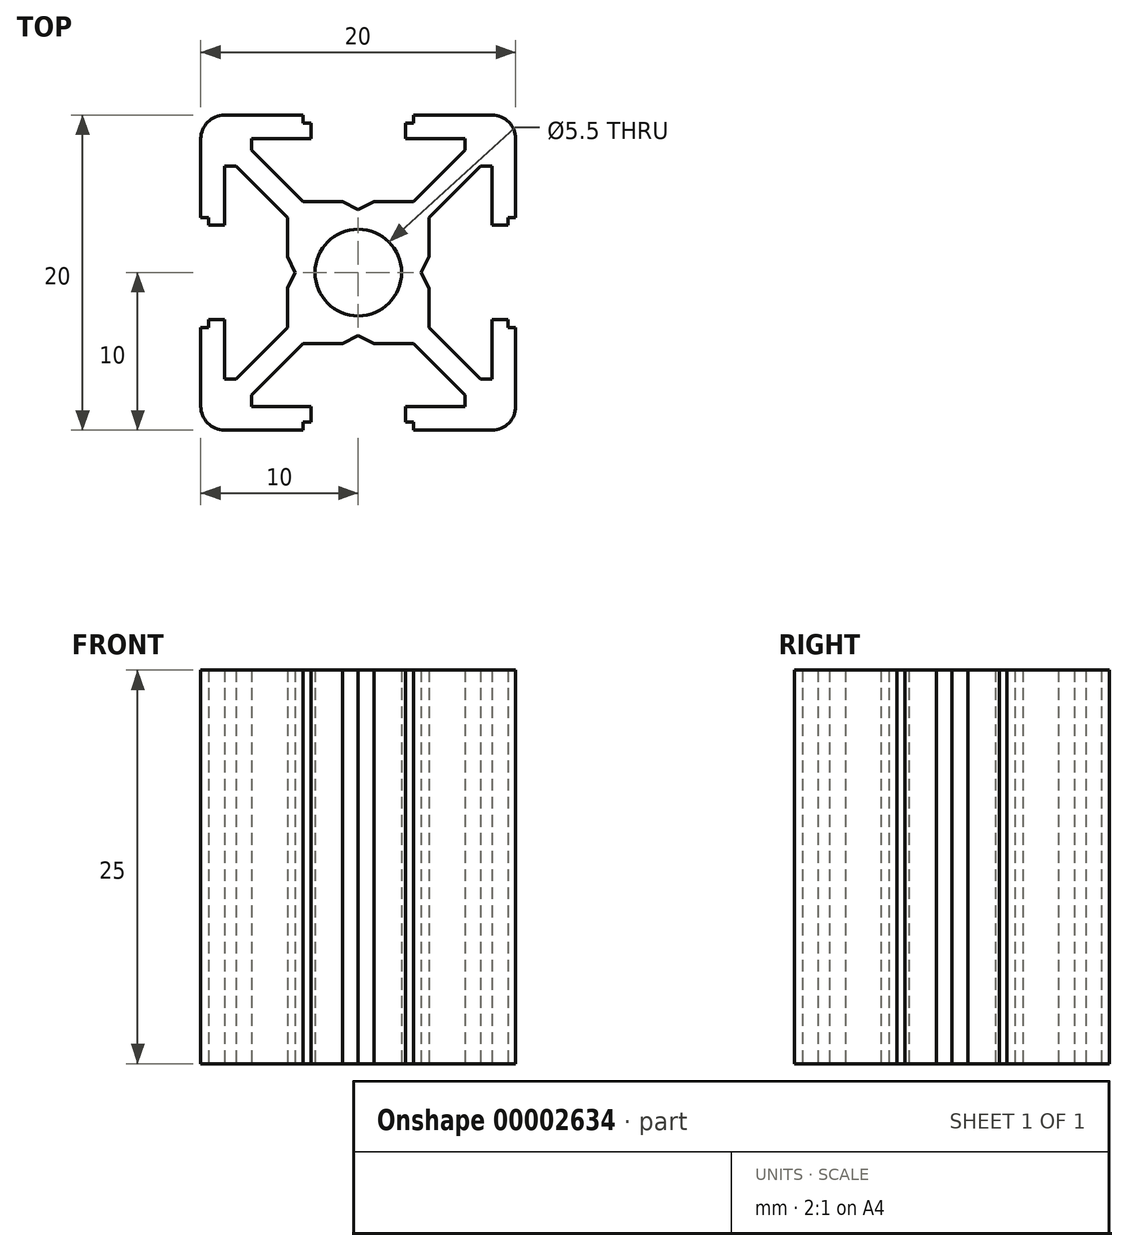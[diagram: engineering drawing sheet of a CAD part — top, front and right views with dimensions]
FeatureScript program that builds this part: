
annotation { "Feature Type Name" : "Feature", "Feature Type Description" : "" }
export const myFeature = defineFeature(function(context is Context, id is Id, definition is map)
    precondition{}
    {
        {
            var Q0;
            Q0=qCreatedBy(makeId("Top.planeOp"),FACE);
            var sketch = newSketch(context, id + "F0", { "sketchPlane" : qUnion([Q0])});
            skLineSegment(sketch, "E0", {"start": v(-1, -4.5) * mm, "end": v(-3.5, -4.5) * mm});
            skLineSegment(sketch, "E1", {"start": v(-6.77, -7.77) * mm, "end": v(-6.77, -8.5) * mm});
            skLineSegment(sketch, "E2", {"start": v(-6.77, -8.5) * mm, "end": v(-3, -8.5) * mm});
            skLineSegment(sketch, "E3", {"start": v(-3, -8.5) * mm, "end": v(-3, -9.5) * mm});
            skLineSegment(sketch, "E4", {"start": v(-5.56, -10) * mm, "end": v(-8.5, -10) * mm});
            skLineSegment(sketch, "E5", {"start": v(-1, -4.5) * mm, "end": v(0, -4) * mm});
            skLineSegment(sketch, "E6", {"start": v(-3, -9.5) * mm, "end": v(-3.5, -9.5) * mm});
            skLineSegment(sketch, "E7", {"start": v(-3.5, -9.5) * mm, "end": v(-3.5, -10) * mm, "construction": true});
            skArc(sketch, "E8.filletArc", {"start": v(-9.56, -9.56) * mm, "mid": v(-9.07, -9.89) * mm, "end": v(-8.5, -10) * mm});
            skLineSegment(sketch, "E9", {"start": v(-3.5, -10) * mm, "end": v(-5.56, -10) * mm});
            skPoint(sketch, "E10.orphan", {"position": v(0, -10) * mm});
            skLineSegment(sketch, "E11.trimOffspring", {"start": v(-8.5, -8.5) * mm, "end": v(-1.94, -1.94) * mm});
            skPoint(sketch, "E12", {"position": v(0, -4.5) * mm});
            skLineSegment(sketch, "E13", {"start": v(-3.5, -4.5) * mm, "end": v(-6.77, -7.77) * mm});
            skArc(sketch, "E14", {"start": v(-1.94, -1.94) * mm, "mid": v(-1.05, -2.54) * mm, "end": v(0, -2.75) * mm});
            skPoint(sketch, "E15", {"position": v(-1.94, -1.94) * mm});
            skLineSegment(sketch, "E16", {"start": v(0, -4) * mm, "end": v(0, -2.75) * mm});
            skLineSegment(sketch, "E17", {"start": v(-9.56, -9.56) * mm, "end": v(-8.5, -8.5) * mm});
            skPoint(sketch, "E18", {"position": v(-5.56, -10) * mm});
            skLineSegment(sketch, "E19", {"start": v(-3.5, -9.5) * mm, "end": v(-3.5, -10) * mm});
            skPoint(sketch, "E20.0.MirrorP", {"position": v(-10, -5.56) * mm});
            skPoint(sketch, "E20.1.MirrorP", {"position": v(-10, -5.56) * mm});
            skPoint(sketch, "E20.2.MirrorP", {"position": v(-10, -5.56) * mm});
            skPoint(sketch, "E20.3.MirrorP", {"position": v(-10, -5.56) * mm});
            skPoint(sketch, "E20.4.MirrorP", {"position": v(-10, -5.56) * mm});
            skPoint(sketch, "E20.5.MirrorP", {"position": v(-10, -5.56) * mm});
            skPoint(sketch, "E20.6.MirrorP", {"position": v(-10, -5.56) * mm});
            skPoint(sketch, "E20.7.MirrorP", {"position": v(-10, -5.56) * mm});
            skPoint(sketch, "E20.8.MirrorP", {"position": v(-10, -5.56) * mm});
            skPoint(sketch, "E20.9.MirrorP", {"position": v(-10, -5.56) * mm});
            skPoint(sketch, "E20.10.MirrorP", {"position": v(-10, -5.56) * mm});
            skLineSegment(sketch, "E20.11.MirrorCS", {"start": v(-9.5, -3.5) * mm, "end": v(-10, -3.5) * mm, "construction": true});
            skPoint(sketch, "E20.12.MirrorP", {"position": v(-10, -5.56) * mm});
            skLineSegment(sketch, "E20.13.MirrorCS", {"start": v(-9.5, -3.5) * mm, "end": v(-10, -3.5) * mm});
            skLineSegment(sketch, "E20.14.MirrorCS", {"start": v(-7.77, -6.77) * mm, "end": v(-8.5, -6.77) * mm});
            skPoint(sketch, "E20.15.MirrorP", {"position": v(-10, -5.56) * mm});
            skLineSegment(sketch, "E20.16.MirrorCS", {"start": v(-9.5, -3) * mm, "end": v(-9.5, -3.5) * mm});
            skPoint(sketch, "E20.17.MirrorP", {"position": v(-10, 0) * mm});
            skLineSegment(sketch, "E20.18.MirrorCS", {"start": v(-10, -5.56) * mm, "end": v(-10, -8.5) * mm});
            skArc(sketch, "E20.19.MirrorCS", {"start": v(-1.94, -1.94) * mm, "mid": v(-2.54, -1.05) * mm, "end": v(-2.75, 0) * mm});
            skPoint(sketch, "E20.20.MirrorP", {"position": v(-4.5, 0) * mm});
            skLineSegment(sketch, "E20.21.MirrorCS", {"start": v(-4.5, -3.5) * mm, "end": v(-7.77, -6.77) * mm});
            skLineSegment(sketch, "E20.23.MirrorCS", {"start": v(-4.5, -1) * mm, "end": v(-4.5, -3.5) * mm});
            skLineSegment(sketch, "E20.24.MirrorCS", {"start": v(-8.5, -6.77) * mm, "end": v(-8.5, -3) * mm});
            skLineSegment(sketch, "E20.25.MirrorCS", {"start": v(-10, -3.5) * mm, "end": v(-10, -5.56) * mm});
            skLineSegment(sketch, "E20.26.MirrorCS", {"start": v(-4, 0) * mm, "end": v(-2.75, 0) * mm});
            skArc(sketch, "E20.28.MirrorCS", {"start": v(-9.56, -9.56) * mm, "mid": v(-9.89, -9.07) * mm, "end": v(-10, -8.5) * mm});
            skLineSegment(sketch, "E20.29.MirrorCS", {"start": v(-4.5, -1) * mm, "end": v(-4, 0) * mm});
            skLineSegment(sketch, "E20.30.MirrorCS", {"start": v(-10, -5.56) * mm, "end": v(-10, -8.5) * mm});
            skPoint(sketch, "E20.31.MirrorP", {"position": v(-10, -5.56) * mm});
            skLineSegment(sketch, "E20.32.MirrorCS", {"start": v(-8.5, -3) * mm, "end": v(-9.5, -3) * mm});
            skPoint(sketch, "E21.0.MirrorP", {"position": v(-5.56, 10) * mm});
            skPoint(sketch, "E21.1.MirrorP", {"position": v(-10, 5.56) * mm});
            skPoint(sketch, "E21.2.MirrorP", {"position": v(-5.56, 10) * mm});
            skPoint(sketch, "E21.3.MirrorP", {"position": v(-10, 5.56) * mm});
            skPoint(sketch, "E21.4.MirrorP", {"position": v(-5.56, 10) * mm});
            skPoint(sketch, "E21.5.MirrorP", {"position": v(-10, 5.56) * mm});
            skPoint(sketch, "E21.6.MirrorP", {"position": v(-10, 5.56) * mm});
            skPoint(sketch, "E21.7.MirrorP", {"position": v(-5.56, 10) * mm});
            skPoint(sketch, "E21.8.MirrorP", {"position": v(-5.56, 10) * mm});
            skPoint(sketch, "E21.9.MirrorP", {"position": v(-10, 5.56) * mm});
            skPoint(sketch, "E21.10.MirrorP", {"position": v(-5.56, 10) * mm});
            skPoint(sketch, "E21.11.MirrorP", {"position": v(-10, 5.56) * mm});
            skPoint(sketch, "E21.12.MirrorP", {"position": v(-5.56, 10) * mm});
            skPoint(sketch, "E21.13.MirrorP", {"position": v(-10, 5.56) * mm});
            skPoint(sketch, "E21.14.MirrorP", {"position": v(-5.56, 10) * mm});
            skPoint(sketch, "E21.15.MirrorP", {"position": v(-10, 5.56) * mm});
            skPoint(sketch, "E21.16.MirrorP", {"position": v(-5.56, 10) * mm});
            skPoint(sketch, "E21.17.MirrorP", {"position": v(-10, 5.56) * mm});
            skLineSegment(sketch, "E21.18.MirrorCS", {"start": v(-9.5, 3.5) * mm, "end": v(-10, 3.5) * mm, "construction": true});
            skPoint(sketch, "E21.19.MirrorP", {"position": v(-5.56, 10) * mm});
            skPoint(sketch, "E21.20.MirrorP", {"position": v(-10, 5.56) * mm});
            skLineSegment(sketch, "E21.21.MirrorCS", {"start": v(-3.5, 9.5) * mm, "end": v(-3.5, 10) * mm, "construction": true});
            skLineSegment(sketch, "E21.22.MirrorCS", {"start": v(-3.5, 9.5) * mm, "end": v(-3.5, 10) * mm});
            skPoint(sketch, "E21.23.MirrorP", {"position": v(-5.56, 10) * mm});
            skLineSegment(sketch, "E21.24.MirrorCS", {"start": v(-9.5, 3.5) * mm, "end": v(-10, 3.5) * mm});
            skPoint(sketch, "E21.25.MirrorP", {"position": v(-10, 5.56) * mm});
            skPoint(sketch, "E21.26.MirrorP", {"position": v(-5.56, 10) * mm});
            skPoint(sketch, "E21.27.MirrorP", {"position": v(-10, 5.56) * mm});
            skLineSegment(sketch, "E21.28.MirrorCS", {"start": v(-3, 9.5) * mm, "end": v(-3.5, 9.5) * mm});
            skLineSegment(sketch, "E21.29.MirrorCS", {"start": v(-9.5, 3) * mm, "end": v(-9.5, 3.5) * mm});
            skLineSegment(sketch, "E21.30.MirrorCS", {"start": v(-8.5, 3) * mm, "end": v(-9.5, 3) * mm});
            skPoint(sketch, "E21.31.MirrorP", {"position": v(-5.56, 10) * mm});
            skPoint(sketch, "E21.32.MirrorP", {"position": v(-10, 5.56) * mm});
            skLineSegment(sketch, "E21.34.MirrorCS", {"start": v(-10, 3.5) * mm, "end": v(-10, 5.56) * mm});
            skArc(sketch, "E21.35.MirrorCS", {"start": v(-9.56, 9.56) * mm, "mid": v(-9.89, 9.07) * mm, "end": v(-10, 8.5) * mm});
            skLineSegment(sketch, "E21.36.MirrorCS", {"start": v(-8.5, 6.77) * mm, "end": v(-8.5, 3) * mm});
            skLineSegment(sketch, "E21.37.MirrorCS", {"start": v(-4.5, 1) * mm, "end": v(-4, 0) * mm});
            skLineSegment(sketch, "E21.38.MirrorCS", {"start": v(-10, 5.56) * mm, "end": v(-10, 8.5) * mm});
            skLineSegment(sketch, "E21.40.MirrorCS", {"start": v(-4.5, 3.5) * mm, "end": v(-7.77, 6.77) * mm});
            skLineSegment(sketch, "E21.41.MirrorCS", {"start": v(-4.5, 1) * mm, "end": v(-4.5, 3.5) * mm});
            skLineSegment(sketch, "E21.42.MirrorCS", {"start": v(-1, 4.5) * mm, "end": v(-3.5, 4.5) * mm});
            skLineSegment(sketch, "E21.43.MirrorCS", {"start": v(-6.77, 8.5) * mm, "end": v(-3, 8.5) * mm});
            skLineSegment(sketch, "E21.44.MirrorCS", {"start": v(-6.77, 7.77) * mm, "end": v(-6.77, 8.5) * mm});
            skLineSegment(sketch, "E21.45.MirrorCS", {"start": v(-5.56, 10) * mm, "end": v(-8.5, 10) * mm});
            skLineSegment(sketch, "E21.46.MirrorCS", {"start": v(-3, 8.5) * mm, "end": v(-3, 9.5) * mm});
            skLineSegment(sketch, "E21.47.MirrorCS", {"start": v(-1, 4.5) * mm, "end": v(0, 4) * mm});
            skLineSegment(sketch, "E21.48.MirrorCS", {"start": v(-5.56, 10) * mm, "end": v(-8.5, 10) * mm});
            skLineSegment(sketch, "E21.49.MirrorCS", {"start": v(-3.5, 10) * mm, "end": v(-5.56, 10) * mm});
            skArc(sketch, "E21.50.MirrorCS", {"start": v(-9.56, 9.56) * mm, "mid": v(-9.07, 9.89) * mm, "end": v(-8.5, 10) * mm});
            skLineSegment(sketch, "E21.51.MirrorCS", {"start": v(-3.5, 4.5) * mm, "end": v(-6.77, 7.77) * mm});
            skLineSegment(sketch, "E21.52.MirrorCS", {"start": v(-8.5, 8.5) * mm, "end": v(-1.94, 1.94) * mm});
            skLineSegment(sketch, "E21.53.MirrorCS", {"start": v(-9.56, 9.56) * mm, "end": v(-8.5, 8.5) * mm});
            skLineSegment(sketch, "E21.54.MirrorCS", {"start": v(-9.56, 9.56) * mm, "end": v(-8.5, 8.5) * mm});
            skLineSegment(sketch, "E21.55.MirrorCS", {"start": v(0, 4) * mm, "end": v(0, 2.75) * mm});
            skArc(sketch, "E21.56.MirrorCS", {"start": v(-1.94, 1.94) * mm, "mid": v(-1.05, 2.54) * mm, "end": v(0, 2.75) * mm});
            skPoint(sketch, "E21.58.MirrorP", {"position": v(0, 4.5) * mm});
            skLineSegment(sketch, "E21.59.MirrorCS", {"start": v(-7.77, 6.77) * mm, "end": v(-8.5, 6.77) * mm});
            skPoint(sketch, "E21.60.MirrorP", {"position": v(-5.56, 10) * mm});
            skArc(sketch, "E21.61.MirrorCS", {"start": v(-1.94, 1.94) * mm, "mid": v(-2.54, 1.05) * mm, "end": v(-2.75, 0) * mm});
            skPoint(sketch, "E21.62.MirrorP", {"position": v(0, 10) * mm});
            skPoint(sketch, "E21.63.MirrorP", {"position": v(-1.94, 1.94) * mm});
            skPoint(sketch, "E21.64.MirrorP", {"position": v(-1.94, 1.94) * mm});
            skLineSegment(sketch, "E21.65.MirrorCS", {"start": v(-10, 5.56) * mm, "end": v(-10, 8.5) * mm});
            skPoint(sketch, "E21.66.MirrorP", {"position": v(-10, 5.56) * mm});
            skPoint(sketch, "E22.0.MirrorP", {"position": v(10, 5.56) * mm});
            skPoint(sketch, "E22.1.MirrorP", {"position": v(5.56, -10) * mm});
            skPoint(sketch, "E22.2.MirrorP", {"position": v(5.56, 10) * mm});
            skPoint(sketch, "E22.3.MirrorP", {"position": v(10, 5.56) * mm});
            skPoint(sketch, "E22.4.MirrorP", {"position": v(10, -5.56) * mm});
            skPoint(sketch, "E22.5.MirrorP", {"position": v(5.56, -10) * mm});
            skPoint(sketch, "E22.6.MirrorP", {"position": v(5.56, -10) * mm});
            skPoint(sketch, "E22.7.MirrorP", {"position": v(10, 5.56) * mm});
            skPoint(sketch, "E22.8.MirrorP", {"position": v(5.56, 10) * mm});
            skPoint(sketch, "E22.9.MirrorP", {"position": v(10, -5.56) * mm});
            skPoint(sketch, "E22.10.MirrorP", {"position": v(10, 5.56) * mm});
            skPoint(sketch, "E22.11.MirrorP", {"position": v(5.56, -10) * mm});
            skPoint(sketch, "E22.12.MirrorP", {"position": v(5.56, 10) * mm});
            skPoint(sketch, "E22.13.MirrorP", {"position": v(10, -5.56) * mm});
            skPoint(sketch, "E22.14.MirrorP", {"position": v(10, 5.56) * mm});
            skPoint(sketch, "E22.15.MirrorP", {"position": v(5.56, -10) * mm});
            skPoint(sketch, "E22.16.MirrorP", {"position": v(10, -5.56) * mm});
            skPoint(sketch, "E22.17.MirrorP", {"position": v(5.56, 10) * mm});
            skPoint(sketch, "E22.18.MirrorP", {"position": v(5.56, -10) * mm});
            skPoint(sketch, "E22.19.MirrorP", {"position": v(5.56, 10) * mm});
            skPoint(sketch, "E22.20.MirrorP", {"position": v(10, 5.56) * mm});
            skPoint(sketch, "E22.21.MirrorP", {"position": v(10, -5.56) * mm});
            skPoint(sketch, "E22.22.MirrorP", {"position": v(10, -5.56) * mm});
            skPoint(sketch, "E22.23.MirrorP", {"position": v(5.56, -10) * mm});
            skPoint(sketch, "E22.24.MirrorP", {"position": v(10, 5.56) * mm});
            skPoint(sketch, "E22.25.MirrorP", {"position": v(5.56, 10) * mm});
            skPoint(sketch, "E22.26.MirrorP", {"position": v(10, -5.56) * mm});
            skPoint(sketch, "E22.27.MirrorP", {"position": v(10, 5.56) * mm});
            skPoint(sketch, "E22.28.MirrorP", {"position": v(5.56, -10) * mm});
            skPoint(sketch, "E22.29.MirrorP", {"position": v(5.56, 10) * mm});
            skPoint(sketch, "E22.30.MirrorP", {"position": v(10, -5.56) * mm});
            skPoint(sketch, "E22.31.MirrorP", {"position": v(5.56, 10) * mm});
            skPoint(sketch, "E22.32.MirrorP", {"position": v(5.56, -10) * mm});
            skPoint(sketch, "E22.33.MirrorP", {"position": v(10, 5.56) * mm});
            skPoint(sketch, "E22.34.MirrorP", {"position": v(10, 5.56) * mm});
            skPoint(sketch, "E22.35.MirrorP", {"position": v(5.56, 10) * mm});
            skPoint(sketch, "E22.36.MirrorP", {"position": v(10, -5.56) * mm});
            skPoint(sketch, "E22.37.MirrorP", {"position": v(5.56, -10) * mm});
            skLineSegment(sketch, "E22.38.MirrorCS", {"start": v(3.5, 9.5) * mm, "end": v(3.5, 10) * mm, "construction": true});
            skLineSegment(sketch, "E22.39.MirrorCS", {"start": v(9.5, 3.5) * mm, "end": v(10, 3.5) * mm, "construction": true});
            skLineSegment(sketch, "E22.40.MirrorCS", {"start": v(9.5, -3.5) * mm, "end": v(10, -3.5) * mm, "construction": true});
            skLineSegment(sketch, "E22.41.MirrorCS", {"start": v(3.5, -9.5) * mm, "end": v(3.5, -10) * mm, "construction": true});
            skPoint(sketch, "E22.42.MirrorP", {"position": v(10, 5.56) * mm});
            skPoint(sketch, "E22.43.MirrorP", {"position": v(10, -5.56) * mm});
            skPoint(sketch, "E22.44.MirrorP", {"position": v(5.56, -10) * mm});
            skPoint(sketch, "E22.45.MirrorP", {"position": v(5.56, 10) * mm});
            skLineSegment(sketch, "E22.46.MirrorCS", {"start": v(9.5, 3.5) * mm, "end": v(10, 3.5) * mm});
            skLineSegment(sketch, "E22.47.MirrorCS", {"start": v(9.5, -3) * mm, "end": v(9.5, -3.5) * mm});
            skLineSegment(sketch, "E22.48.MirrorCS", {"start": v(9.5, -3.5) * mm, "end": v(10, -3.5) * mm});
            skLineSegment(sketch, "E22.49.MirrorCS", {"start": v(9.56, -9.56) * mm, "end": v(8.5, -8.5) * mm});
            skLineSegment(sketch, "E22.50.MirrorCS", {"start": v(3, -9.5) * mm, "end": v(3.5, -9.5) * mm});
            skPoint(sketch, "E22.51.MirrorP", {"position": v(10, -5.56) * mm});
            skPoint(sketch, "E22.52.MirrorP", {"position": v(10, 5.56) * mm});
            skPoint(sketch, "E22.53.MirrorP", {"position": v(5.56, 10) * mm});
            skPoint(sketch, "E22.54.MirrorP", {"position": v(5.56, -10) * mm});
            skLineSegment(sketch, "E22.55.MirrorCS", {"start": v(3, 9.5) * mm, "end": v(3.5, 9.5) * mm});
            skLineSegment(sketch, "E22.56.MirrorCS", {"start": v(9.5, 3) * mm, "end": v(9.5, 3.5) * mm});
            skLineSegment(sketch, "E22.57.MirrorCS", {"start": v(3.5, -9.5) * mm, "end": v(3.5, -10) * mm});
            skLineSegment(sketch, "E22.58.MirrorCS", {"start": v(3.5, 9.5) * mm, "end": v(3.5, 10) * mm});
            skLineSegment(sketch, "E22.59.MirrorCS", {"start": v(3, 8.5) * mm, "end": v(3, 9.5) * mm});
            skLineSegment(sketch, "E22.60.MirrorCS", {"start": v(6.77, 7.77) * mm, "end": v(6.77, 8.5) * mm});
            skPoint(sketch, "E22.61.MirrorP", {"position": v(5.56, 10) * mm});
            skLineSegment(sketch, "E22.62.MirrorCS", {"start": v(6.77, -7.77) * mm, "end": v(6.77, -8.5) * mm});
            skPoint(sketch, "E22.63.MirrorP", {"position": v(5.56, -10) * mm});
            skPoint(sketch, "E22.64.MirrorP", {"position": v(10, -5.56) * mm});
            skLineSegment(sketch, "E22.65.MirrorCS", {"start": v(9.56, -9.56) * mm, "end": v(8.5, -8.5) * mm});
            skLineSegment(sketch, "E22.66.MirrorCS", {"start": v(7.77, 6.77) * mm, "end": v(8.5, 6.77) * mm});
            skLineSegment(sketch, "E22.67.MirrorCS", {"start": v(1, 4.5) * mm, "end": v(0, 4) * mm});
            skLineSegment(sketch, "E22.68.MirrorCS", {"start": v(4.5, -1) * mm, "end": v(4, 0) * mm});
            skLineSegment(sketch, "E22.69.MirrorCS", {"start": v(4, 0) * mm, "end": v(2.75, 0) * mm});
            skLineSegment(sketch, "E22.70.MirrorCS", {"start": v(1, -4.5) * mm, "end": v(0, -4) * mm});
            skLineSegment(sketch, "E22.71.MirrorCS", {"start": v(10, 5.56) * mm, "end": v(10, 8.5) * mm});
            skPoint(sketch, "E22.72.MirrorP", {"position": v(10, 5.56) * mm});
            skPoint(sketch, "E22.73.MirrorP", {"position": v(10, 0) * mm});
            skLineSegment(sketch, "E22.74.MirrorCS", {"start": v(9.56, 9.56) * mm, "end": v(8.5, 8.5) * mm});
            skLineSegment(sketch, "E22.75.MirrorCS", {"start": v(4.5, 1) * mm, "end": v(4, 0) * mm});
            skLineSegment(sketch, "E22.76.MirrorCS", {"start": v(7.77, -6.77) * mm, "end": v(8.5, -6.77) * mm});
            skLineSegment(sketch, "E22.78.MirrorCS", {"start": v(10, 5.56) * mm, "end": v(10, 8.5) * mm});
            skLineSegment(sketch, "E22.79.MirrorCS", {"start": v(3.5, -10) * mm, "end": v(5.56, -10) * mm});
            skLineSegment(sketch, "E22.80.MirrorCS", {"start": v(3, -8.5) * mm, "end": v(3, -9.5) * mm});
            skLineSegment(sketch, "E22.81.MirrorCS", {"start": v(5.56, -10) * mm, "end": v(8.5, -10) * mm});
            skPoint(sketch, "E22.83.MirrorP", {"position": v(5.56, -10) * mm});
            skLineSegment(sketch, "E22.84.MirrorCS", {"start": v(8.5, 3) * mm, "end": v(9.5, 3) * mm});
            skLineSegment(sketch, "E22.85.MirrorCS", {"start": v(3.5, 10) * mm, "end": v(5.56, 10) * mm});
            skArc(sketch, "E22.86.MirrorCS", {"start": v(1.94, -1.94) * mm, "mid": v(1.05, -2.54) * mm, "end": v(0, -2.75) * mm});
            skPoint(sketch, "E22.87.MirrorP", {"position": v(1.94, -1.94) * mm});
            skPoint(sketch, "E22.88.MirrorP", {"position": v(4.5, 0) * mm});
            skArc(sketch, "E22.89.MirrorCS", {"start": v(9.56, 9.56) * mm, "mid": v(9.07, 9.89) * mm, "end": v(8.5, 10) * mm});
            skLineSegment(sketch, "E22.90.MirrorCS", {"start": v(10, 3.5) * mm, "end": v(10, 5.56) * mm});
            skLineSegment(sketch, "E22.91.MirrorCS", {"start": v(8.5, -8.5) * mm, "end": v(1.94, -1.94) * mm});
            skLineSegment(sketch, "E22.92.MirrorCS", {"start": v(3.5, -4.5) * mm, "end": v(6.77, -7.77) * mm});
            skArc(sketch, "E22.93.MirrorCS", {"start": v(9.56, -9.56) * mm, "mid": v(9.07, -9.89) * mm, "end": v(8.5, -10) * mm});
            skLineSegment(sketch, "E22.94.MirrorCS", {"start": v(6.77, 8.5) * mm, "end": v(3, 8.5) * mm});
            skLineSegment(sketch, "E22.95.MirrorCS", {"start": v(4.5, 1) * mm, "end": v(4.5, 3.5) * mm});
            skLineSegment(sketch, "E22.96.MirrorCS", {"start": v(10, -5.56) * mm, "end": v(10, -8.5) * mm});
            skLineSegment(sketch, "E22.97.MirrorCS", {"start": v(5.56, -10) * mm, "end": v(8.5, -10) * mm});
            skPoint(sketch, "E22.99.MirrorP", {"position": v(5.56, 10) * mm});
            skLineSegment(sketch, "E22.101.MirrorCS", {"start": v(10, -5.56) * mm, "end": v(10, -8.5) * mm});
            skPoint(sketch, "E22.103.MirrorP", {"position": v(4.5, 0) * mm});
            skArc(sketch, "E22.104.MirrorCS", {"start": v(1.94, 1.94) * mm, "mid": v(1.05, 2.54) * mm, "end": v(0, 2.75) * mm});
            skArc(sketch, "E22.105.MirrorCS", {"start": v(1.94, -1.94) * mm, "mid": v(2.54, -1.05) * mm, "end": v(2.75, 0) * mm});
            skLineSegment(sketch, "E22.106.MirrorCS", {"start": v(4.5, 3.5) * mm, "end": v(7.77, 6.77) * mm});
            skLineSegment(sketch, "E22.107.MirrorCS", {"start": v(8.5, 8.5) * mm, "end": v(1.94, 1.94) * mm});
            skLineSegment(sketch, "E22.108.MirrorCS", {"start": v(8.5, -6.77) * mm, "end": v(8.5, -3) * mm});
            skArc(sketch, "E22.109.MirrorCS", {"start": v(9.56, -9.56) * mm, "mid": v(9.89, -9.07) * mm, "end": v(10, -8.5) * mm});
            skPoint(sketch, "E22.110.MirrorP", {"position": v(1.94, 1.94) * mm});
            skLineSegment(sketch, "E22.111.MirrorCS", {"start": v(6.77, -8.5) * mm, "end": v(3, -8.5) * mm});
            skLineSegment(sketch, "E22.112.MirrorCS", {"start": v(1, -4.5) * mm, "end": v(3.5, -4.5) * mm});
            skLineSegment(sketch, "E22.113.MirrorCS", {"start": v(4.5, -1) * mm, "end": v(4.5, -3.5) * mm});
            skLineSegment(sketch, "E22.114.MirrorCS", {"start": v(3.5, 4.5) * mm, "end": v(6.77, 7.77) * mm});
            skPoint(sketch, "E22.115.MirrorP", {"position": v(10, -5.56) * mm});
            skLineSegment(sketch, "E22.116.MirrorCS", {"start": v(9.56, 9.56) * mm, "end": v(8.5, 8.5) * mm});
            skLineSegment(sketch, "E22.117.MirrorCS", {"start": v(4, 0) * mm, "end": v(2.75, 0) * mm});
            skArc(sketch, "E22.118.MirrorCS", {"start": v(9.56, 9.56) * mm, "mid": v(9.89, 9.07) * mm, "end": v(10, 8.5) * mm});
            skPoint(sketch, "E22.119.MirrorP", {"position": v(5.56, 10) * mm});
            skLineSegment(sketch, "E22.120.MirrorCS", {"start": v(8.5, -3) * mm, "end": v(9.5, -3) * mm});
            skLineSegment(sketch, "E22.121.MirrorCS", {"start": v(1, 4.5) * mm, "end": v(3.5, 4.5) * mm});
            skArc(sketch, "E22.122.MirrorCS", {"start": v(1.94, 1.94) * mm, "mid": v(2.54, 1.05) * mm, "end": v(2.75, 0) * mm});
            skLineSegment(sketch, "E22.123.MirrorCS", {"start": v(5.56, 10) * mm, "end": v(8.5, 10) * mm});
            skPoint(sketch, "E22.124.MirrorP", {"position": v(10, 0) * mm});
            skLineSegment(sketch, "E22.125.MirrorCS", {"start": v(10, -3.5) * mm, "end": v(10, -5.56) * mm});
            skLineSegment(sketch, "E22.126.MirrorCS", {"start": v(5.56, 10) * mm, "end": v(8.5, 10) * mm});
            skLineSegment(sketch, "E22.127.MirrorCS", {"start": v(4.5, -3.5) * mm, "end": v(7.77, -6.77) * mm});
            skPoint(sketch, "E22.128.MirrorP", {"position": v(10, -5.56) * mm});
            skPoint(sketch, "E22.129.MirrorP", {"position": v(1.94, -1.94) * mm});
            skPoint(sketch, "E22.131.MirrorP", {"position": v(1.94, 1.94) * mm});
            skLineSegment(sketch, "E22.132.MirrorCS", {"start": v(8.5, 6.77) * mm, "end": v(8.5, 3) * mm});
            skPoint(sketch, "E22.133.MirrorP", {"position": v(10, 5.56) * mm});
            skSolve(sketch);
        }
        {
            var Q0;
            Q0=qSketchRegion(id+"F0",true);
            extrude(context, id + "F1", {"entities" : qUnion([Q0]), "depth" : 25 * mm});
        }
    });
